# Revit family: NBS_Allermuir_OffcChrs_Kin_LowBackStool
name_source: partatom
category: Furniture
revit_build: Autodesk Revit 2018 (Build: 20190510_1515(x64)
units: mm (PartAtom-declared; Revit-internal decimal feet)

## family parameters
Always vertical = Yes
Cut with Voids When Loaded = No
Room Calculation Point = No
Shared = No
Work Plane-Based = No

## types (2) — shared parameters
AssetType = Movable
Category = Pr_40_50_12_57:Office chairs
CodePerformance = ANSI/BIFMA X5.1-2017
Color = Off-Black, White, Crayon Grey, Pistachio, Haze Blue, Aubergine, Seattle Green, Red
DurationUnit = year
ExpectedLife = 10
Finish = Off-Black, White, Crayon Grey, Pistachio, Haze Blue, Aubergine, Seattle Green, Red
FrameMountingMaterial = NBS_Allermuir_Plastic_Black
IfcExportAs = IfcFurnitureType
IfcExportType = STOOL
IsBuiltIn = No
LegConnectorFrameMaterial = NBS_Allermuir_Steel_BlackPowderCoat
ManufacturerName = Allermuir
ManufacturerURL = www.allermuir.co.uk
ModelReference = Kin_LowBackStool
NBSCertification = www.nationalbimlibrary.com/cert/qxsafnkd
NBSDescription = Office chairs
NBSReference = 45-35-20/330
NominalLength = 445 mm  [stored 1.45997 ft]
NominalWidth = 445 mm  [stored 1.45997 ft]
PlasticAndMetalFinish = Off-Black, White, Crayon Grey, Pistachio, Haze Blue, Aubergine, Seattle Green, Red
ProductInformation = https://www.allermuir.com
SeatDepth = 355 mm
SeatMaterial = NBS_Allermuir_Plastic_Black
SeatWidth = 410 mm
Status = UNSET
Style = Stool
SustainabilityPerformance = 99% recyclable
Uniclass2015Code = Pr_40_50_12_57
Uniclass2015Title = Office chairs
Uniclass2015Version = Products v1.15
Version = 1
WarrantyDescription = Allermuir warrant that its manufactured products are free from manufacturing defects - in materials or workmanship - for a period of five (5) years. , Allermuir will repair, or replace (at Allermuir's sole discretion) with comparable free of charge materials / components, any product / component which fails under normal use in a single shift environment, as a result of a defect in the materials and/ or workmanship
WarrantyDurationParts = 5
WarrantyDurationUnit = year
zero-valued in all types: HighestSeatingHeight, LowestSeatingHeight

## per-type parameters (varying)
| type | BIMObjectName | Description | Features | FrameFinish | FrameMaterial | FrameType | Material | ModelNumber | Name | NominalDepth | NominalHeight | SeatingHeight | Size | WoodStains |
| Kin_LowBackStool_KIN502 | NBS_Allermuir_OfficeChairs_Kin_LowBackStool_KIN502 | Low back stool on 4 leg frame | Plastic shell — Colour: Off-Black, Tubular steel frame finished in Off-Black powder coat, Footrest protector, Plastic glides, Counter height option available, Plastic glides with felt | Off-Black, White, Crayon Grey, Pistachio, Haze Blue, Aubergine, Seattle Green, Red | NBS_Allermuir_Steel_BlackPowderCoat | NBS_Allermuir_OffcChrs_Kin_LowBackStool_4LegFrame : 4LegFrame | Polypropylene, Aluminium Casting | KIN502 | OfficeChairs_KIN502_Kin_Allermuir | 460 mm  [stored 1.50919 ft] | 885 mm | 745 mm  [stored 2.44423 ft] | 460 x 885 x 745 mm |  |
| Kin_LowBackStool_KIN503 | NBS_Allermuir_OfficeChairs_Kin_LowBackStool_KIN503 | Low back stool on wooden legs | Plastic shell — Colour: Off-Black, Aluminium leg connector frame finished in Off-Black powder coat, Solid Ash legs with a clear finish, Footrest finished in Off-Black powdercoat, Footrest protector, Plastic glides, Counter height option available, Plastic glides with felt | Clear Ash (standard), Clear Oak, Wenge (wood stain), Dark Walnut (wood stain), American Walnut (wood stain), American Cherry (wood stain), Off Black (colour wash) ,Off Black (colour wash), White (colour wash), Crayon Grey(colour wash), Pistachio (colour wash), Seattle Green (colour wash), Aubergine (colour wash), Red (colour wash), Haze Blue (colour wash), | NBS_Allermuir_Ash_ClearFinish | NBS_Allermuir_OffcChrs_Kin_LowBackStool_WoodLegs : WoodLegs | Polypropylene, Aluminium Casting, Solid Wood | KIN503 | OfficeChairs_KIN503_Kin_Allermuir | 480 mm  [stored 1.5748 ft] | 880 mm  [stored 2.88714 ft] | 740 mm  [stored 2.42782 ft] | 480 x 880 x 445 mm | Clear Ash (standard), Clear Oak, Wenge (wood stain), Dark Walnut (wood stain), American Walnut (wood stain), American Cherry (wood stain), Off Black (colour wash) ,Off Black (colour wash), White (colour wash), Crayon Grey(colour wash), Pistachio (colour wash), Seattle Green (colour wash), Aubergine (colour wash), Red (colour wash), Haze Blue (colour wash), |

note: [stored X ft] marks values corroborated as IEEE doubles in the binary element streams (Revit-internal decimal feet)

## geometry (parser evidence)
native form markers: Sweep x12
no freeform markers — native parametric forms only
